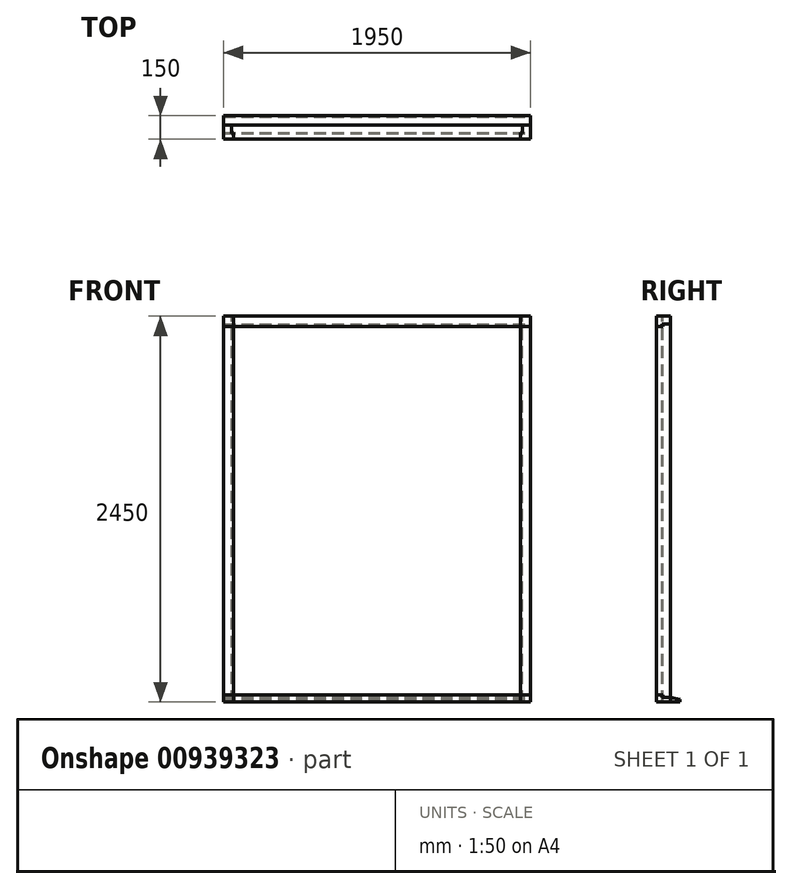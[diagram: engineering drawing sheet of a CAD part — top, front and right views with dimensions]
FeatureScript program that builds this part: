
annotation { "Feature Type Name" : "Feature", "Feature Type Description" : "" }
export const myFeature = defineFeature(function(context is Context, id is Id, definition is map)
    precondition{}
    {
        {
            var Q0;
            Q0=qCreatedBy(makeId("Right.planeOp"),FACE);
            var sketch = newSketch(context, id + "F0", { "sketchPlane" : qUnion([Q0])});
            skPoint(sketch, "E0.end.orphan", {"position": v(150, 0) * mm});
            skLineSegment(sketch, "E1", {"start": v(150, 15) * mm, "end": v(150, 0) * mm});
            skLineSegment(sketch, "E2", {"start": v(0, 0) * mm, "end": v(139, 0) * mm});
            skArc(sketch, "E3", {"start": v(145, 0) * mm, "mid": v(142, 3) * mm, "end": v(139, 0) * mm});
            skLineSegment(sketch, "E4.trimOffspring", {"start": v(145, 0) * mm, "end": v(150, 0) * mm});
            skLineSegment(sketch, "E5.top", {"start": v(0, 45) * mm, "end": v(42, 45) * mm});
            skLineSegment(sketch, "E6.top", {"start": v(42, 30) * mm, "end": v(90, 30) * mm});
            skLineSegment(sketch, "E6.left", {"start": v(42, 45) * mm, "end": v(42, 32.84) * mm});
            skPoint(sketch, "E7.start.orphan", {"position": v(90, 30) * mm});
            skLineSegment(sketch, "E8", {"start": v(90, 30) * mm, "end": v(150, 15) * mm});
            skLineSegment(sketch, "E9", {"start": v(42, 45) * mm, "end": v(0, 45) * mm});
            skLineSegment(sketch, "E10", {"start": v(0, 45) * mm, "end": v(0, 0) * mm});
            skLineSegment(sketch, "E11.bottom", {"start": v(42, 30) * mm, "end": v(36, 30) * mm});
            skLineSegment(sketch, "E11.top", {"start": v(42, 32.84) * mm, "end": v(36, 32.84) * mm});
            skLineSegment(sketch, "E11.right", {"start": v(36, 30) * mm, "end": v(36, 32.84) * mm});
            skLineSegment(sketch, "E12.bottom", {"start": v(0, 2450) * mm, "end": v(90, 2450) * mm});
            skLineSegment(sketch, "E12.left", {"start": v(0, 2450) * mm, "end": v(0, 2385) * mm});
            skLineSegment(sketch, "E13", {"start": v(90, 2450) * mm, "end": v(90, 2400) * mm});
            skLineSegment(sketch, "E14", {"start": v(90, 2400) * mm, "end": v(42, 2400) * mm});
            skLineSegment(sketch, "E15", {"start": v(42, 2397.13) * mm, "end": v(42, 2385) * mm});
            skLineSegment(sketch, "E16", {"start": v(42, 2385) * mm, "end": v(0, 2385) * mm});
            skLineSegment(sketch, "E17.bottom", {"start": v(42, 2400) * mm, "end": v(36, 2400) * mm});
            skLineSegment(sketch, "E17.top", {"start": v(42, 2397.13) * mm, "end": v(36, 2397.13) * mm});
            skLineSegment(sketch, "E17.right", {"start": v(36, 2400) * mm, "end": v(36, 2397.13) * mm});
            skSolve(sketch);
        }
        {
            var Q0;
            Q0 = qSketchRegion(id + "F0", true);
            extrude(context, id + "F1", {"entities" : qUnion([Q0]), "oppositeDirection" : true, "depth" : 1950 * mm, "offsetDistance" : 25 * mm});
        }
        {
            var Q0;
            Q0=makeQuery(id+"F1.opExtrude","SWEPT_FACE",FACE,{"disambiguationData":[OSD([sQuery(id+"F0.wireOp",EDGE,"E12.bottom")])]});
            var sketch = newSketch(context, id + "F2", { "sketchPlane" : qUnion([Q0])});
            skLineSegment(sketch, "E18", {"start": v(-1950, 0) * mm, "end": v(-1885, 0) * mm});
            skLineSegment(sketch, "E19", {"start": v(-1885, 0) * mm, "end": v(-1885, 42) * mm});
            skLineSegment(sketch, "E20", {"start": v(-1885, 42) * mm, "end": v(-1897.25, 42) * mm});
            skLineSegment(sketch, "E21", {"start": v(-1900, 42) * mm, "end": v(-1900, 90) * mm});
            skLineSegment(sketch, "E22", {"start": v(-1900, 90) * mm, "end": v(-1950, 90) * mm});
            skLineSegment(sketch, "E23", {"start": v(-1950, 90) * mm, "end": v(-1950, 0) * mm});
            skLineSegment(sketch, "E24.top", {"start": v(-1900, 36) * mm, "end": v(-1897.25, 36) * mm});
            skLineSegment(sketch, "E24.left", {"start": v(-1900, 42) * mm, "end": v(-1900, 36) * mm});
            skLineSegment(sketch, "E24.right", {"start": v(-1897.25, 42) * mm, "end": v(-1897.25, 36) * mm});
            skLineSegment(sketch, "E25", {"start": v(0, 0) * mm, "end": v(-65, 0) * mm});
            skLineSegment(sketch, "E26", {"start": v(-65, 0) * mm, "end": v(-65, 42) * mm});
            skLineSegment(sketch, "E27", {"start": v(-65, 42) * mm, "end": v(-52.8, 42) * mm});
            skLineSegment(sketch, "E28", {"start": v(-50, 42) * mm, "end": v(-50, 90) * mm});
            skLineSegment(sketch, "E29", {"start": v(-50, 90) * mm, "end": v(0, 90) * mm});
            skLineSegment(sketch, "E30", {"start": v(0, 90) * mm, "end": v(0, 0) * mm});
            skLineSegment(sketch, "E31.top", {"start": v(-50, 36) * mm, "end": v(-52.8, 36) * mm});
            skLineSegment(sketch, "E31.left", {"start": v(-50, 42) * mm, "end": v(-50, 36) * mm});
            skLineSegment(sketch, "E31.right", {"start": v(-52.8, 42) * mm, "end": v(-52.8, 36) * mm});
            skSolve(sketch);
        }
        {
            var Q0;
            Q0 = qSketchRegion(id + "F2", true);
            extrude(context, id + "F3", {"entities" : qUnion([Q0]), "oppositeDirection" : true, "depth" : 2450 * mm, "offsetDistance" : 25 * mm});
        }
    });
